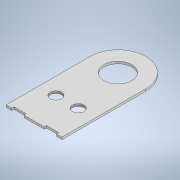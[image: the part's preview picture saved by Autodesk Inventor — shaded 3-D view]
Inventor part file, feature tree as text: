
AUTODESK INVENTOR PART (.ipt)
format: ipt  version: 2022 (Build 260153000, 153)  size: 139,776 bytes
history: native  units: mm
features: sheet_metal_op x1, sketch x1, other x1
ambient origin geometry x8: Origin, YZ Plane, XZ Plane, XY Plane, X Axis, Y Axis, Z Axis, Center Point
bodies: Body1 (feature_tree)
feature tree (3):
  sheet_metal_op  "Face2"
  sketch  "Sketch1"  dims[d0=10.2mm d1=25.0mm d2=2.0mm d3=2.0mm d6=5.0mm d7=11.0mm d8=5.0mm d9=11.0mm d10=50.0mm d12=25.0mm d13=100.0mm d14=29.5mm d16=10.2mm d17=29.5mm d18=20.0mm d19=15.0mm d20=2.0mm]
  other  "Plate2"
